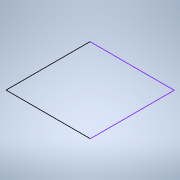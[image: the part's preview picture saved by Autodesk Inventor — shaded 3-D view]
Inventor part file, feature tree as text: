
AUTODESK INVENTOR PART (.ipt)
format: ipt  version: 2022.3 (Build 263350000, 350)  size: 120,320 bytes
history: native  units: mm
features: extrude x3, sketch x3, other x3, thicken_offset x2, plane x1, reference x1
ambient origin geometry x8: Origin, YZ Plane, XZ Plane, XY Plane, X Axis, Y Axis, Z Axis, Center Point
bodies: Solid1 (feature_tree)
feature tree (13):
  plane  "Work Plane1"
  extrude  "Extrusion1"  Depth=8.0mm
  extrude  "Extrusion2"  Depth=0.2mm
  thicken_offset  "Thicken1"
  thicken_offset  "Thicken2"
  sketch  "Sketch3"  dims[d6=0.2mm d7=0.2mm d8=0.2mm d9=10.0mm d10=0.0mm]
  other  "Work Point1"
  extrude  "Extrusion3"  Depth=10.0mm
  sketch  "Sketch1"  dims[d0=8.0mm d1=0.0mm d2=6.0mm]
  reference  "Reference1"
  sketch  "Sketch2"  dims[d3=15.981mm d4=0.0mm d5=0.2mm]
  other  "v2.0.iam"
  other  "Base:1"
